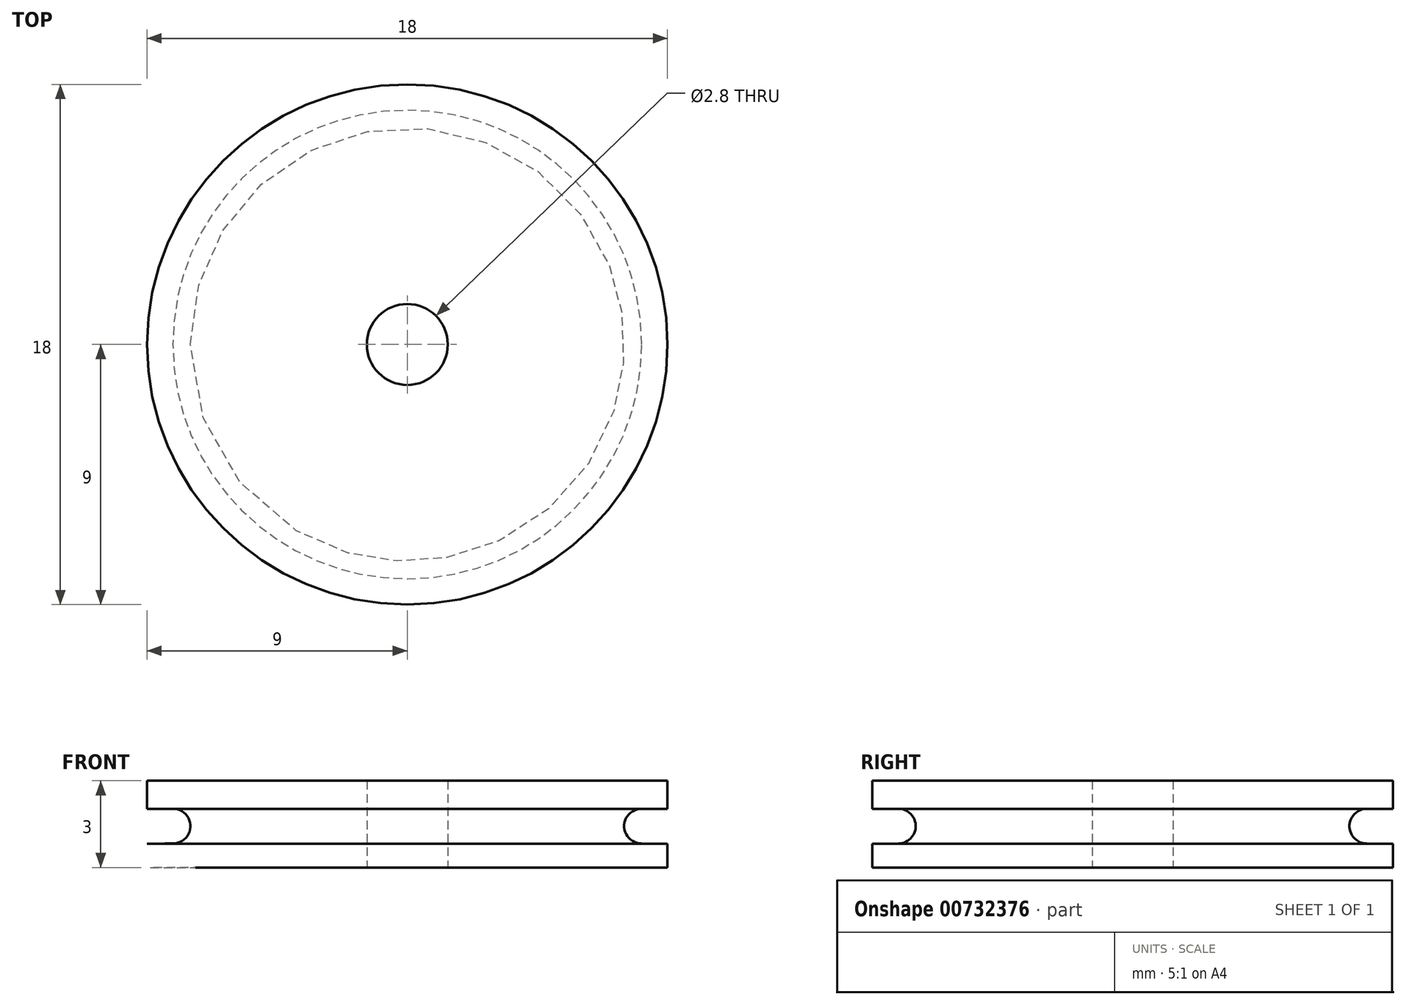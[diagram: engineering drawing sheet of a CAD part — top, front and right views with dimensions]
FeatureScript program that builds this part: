
annotation { "Feature Type Name" : "Feature", "Feature Type Description" : "" }
export const myFeature = defineFeature(function(context is Context, id is Id, definition is map)
    precondition{}
    {
        {
            var Q0;
            Q0=qCreatedBy(makeId("Top.planeOp"),FACE);
            var sketch = newSketch(context, id + "F0", { "sketchPlane" : qUnion([Q0])});
            skCircle(sketch, "E0", {"center": v(-25.06, 15.77) * mm, "radius": 1.4 * mm});
            skCircle(sketch, "E1", {"center": v(-25.06, 15.77) * mm, "radius": 9 * mm});
            skSolve(sketch);
        }
        {
            var Q0;
            Q0=makeQuery(id+"F0.imprint","IMPRINT",FACE,{"disambiguationData":[TD([[makeQuery(id+"F0.imprint","IMPRINT",EDGE,{"derivedFrom":sQuery(id+"F0.wireOp",EDGE,"E0")}),-1.0]])]});
            extrude(context, id + "F1", {"entities" : qUnion([Q0]), "depth" : 3 * mm, "offsetDistance" : 25.4 * mm});
        }
        {
            var Q0;
            Q0=qCreatedBy(makeId("Right.planeOp"),FACE);
            var sketch = newSketch(context, id + "F2", { "sketchPlane" : qUnion([Q0])});
            skCircle(sketch, "E2", {"center": v(-8.1, 1.43) * mm, "radius": 0.6 * mm});
            skLineSegment(sketch, "E3", {"start": v(-8.1, 2.03) * mm, "end": v(-10.5, 2.03) * mm});
            skLineSegment(sketch, "E4", {"start": v(-8.1, 0.83) * mm, "end": v(-10.5, 0.8) * mm});
            skLineSegment(sketch, "E5", {"start": v(-10.5, 0.8) * mm, "end": v(-10.5, 2.03) * mm});
            skSolve(sketch);
        }
        {
            var Q0;
            Q0=makeQuery(id+"F1.opExtrude","SWEPT_BODY",BODY,{"disambiguationData":[OSD([sQuery(id+"F0.wireOp",EDGE,"E0"),sQuery(id+"F0.wireOp",EDGE,"E1")])]});
            transform(context, id + "F3", {"entities" : qUnion([Q0]), "transformType" : TransformType.TRANSLATION_3D, "dx" : 25.17 * mm, "dy" : 0 * mm, "dz" : 0 * mm, "makeCopy" : false});
        }
        {
            var Q0;
            Q0=makeQuery(id+"F1.opExtrude","SWEPT_BODY",BODY,{"disambiguationData":[OSD([sQuery(id+"F0.wireOp",EDGE,"E0"),sQuery(id+"F0.wireOp",EDGE,"E1")])]});
            transform(context, id + "F4", {"entities" : qUnion([Q0]), "transformType" : TransformType.TRANSLATION_3D, "dx" : -0.1 * mm, "dy" : -15.77 * mm, "dz" : 0 * mm, "makeCopy" : false});
        }
        {
            var Q0;
            Q0=qCreatedBy(makeId("Right.planeOp"),FACE);
            var sketch = newSketch(context, id + "F5", { "sketchPlane" : qUnion([Q0])});
            skLineSegment(sketch, "E6", {"start": v(0, 5.92) * mm, "end": v(0, -2) * mm});
            skSolve(sketch);
        }
        {
            var Q0;
            Q0=makeQuery(id+"F2.imprint","IMPRINT",FACE,{"disambiguationData":[TD([[makeQuery(id+"F2.imprint","IMPRINT",EDGE,{"derivedFrom":sQuery(id+"F2.wireOp",EDGE,"E2")}),1.0]])]});
            var Q1;
            {var subQ0=sQuery(id+"F2.wireOp",EDGE,"E3");Q1=makeQuery(id+"F2.imprint","IMPRINT",FACE,{"disambiguationData":[TD([[makeQuery(id+"F2.imprint","IMPRINT",EDGE,{"derivedFrom":subQ0}),1.0]])]});}
            var Q2;
            Q2=sQuery(id+"F5.wireOp",EDGE,"E6");
            revolve(context, id + "F6", {"operationType" : NewBodyOperationType.REMOVE, "surfaceOperationType" : NewSurfaceOperationType.NEW, "entities" : qUnion([Q0, Q1]), "axis" : qUnion([Q2]), "revolveType" : RevolveType.FULL, "oppositeDirection" : true});
        }
    });
